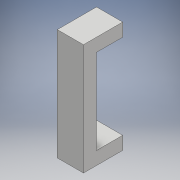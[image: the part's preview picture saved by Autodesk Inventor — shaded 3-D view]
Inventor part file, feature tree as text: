
AUTODESK INVENTOR PART (.ipt)
format: ipt  version: 2017 (Build 210142000, 142)  size: 104,960 bytes
history: native  units: mm
features: extrude x2, sketch x2
ambient origin geometry x8: Origin, YZ Plane, XZ Plane, XY Plane, X Axis, Y Axis, Z Axis, Center Point
bodies: Solid1 (feature_tree)
feature tree (4):
  extrude  "Extrusion1"  Depth=85.0mm
  extrude  "Extrusion2"  Depth=10.0mm
  sketch  "Sketch1"  dims[d0=20.0mm d1=85.0mm]
  sketch  "Sketch2"  dims[d2=10.0mm d3=0.0mm d4=10.0mm d5=10.0mm d6=20.0mm d7=0.0mm]
